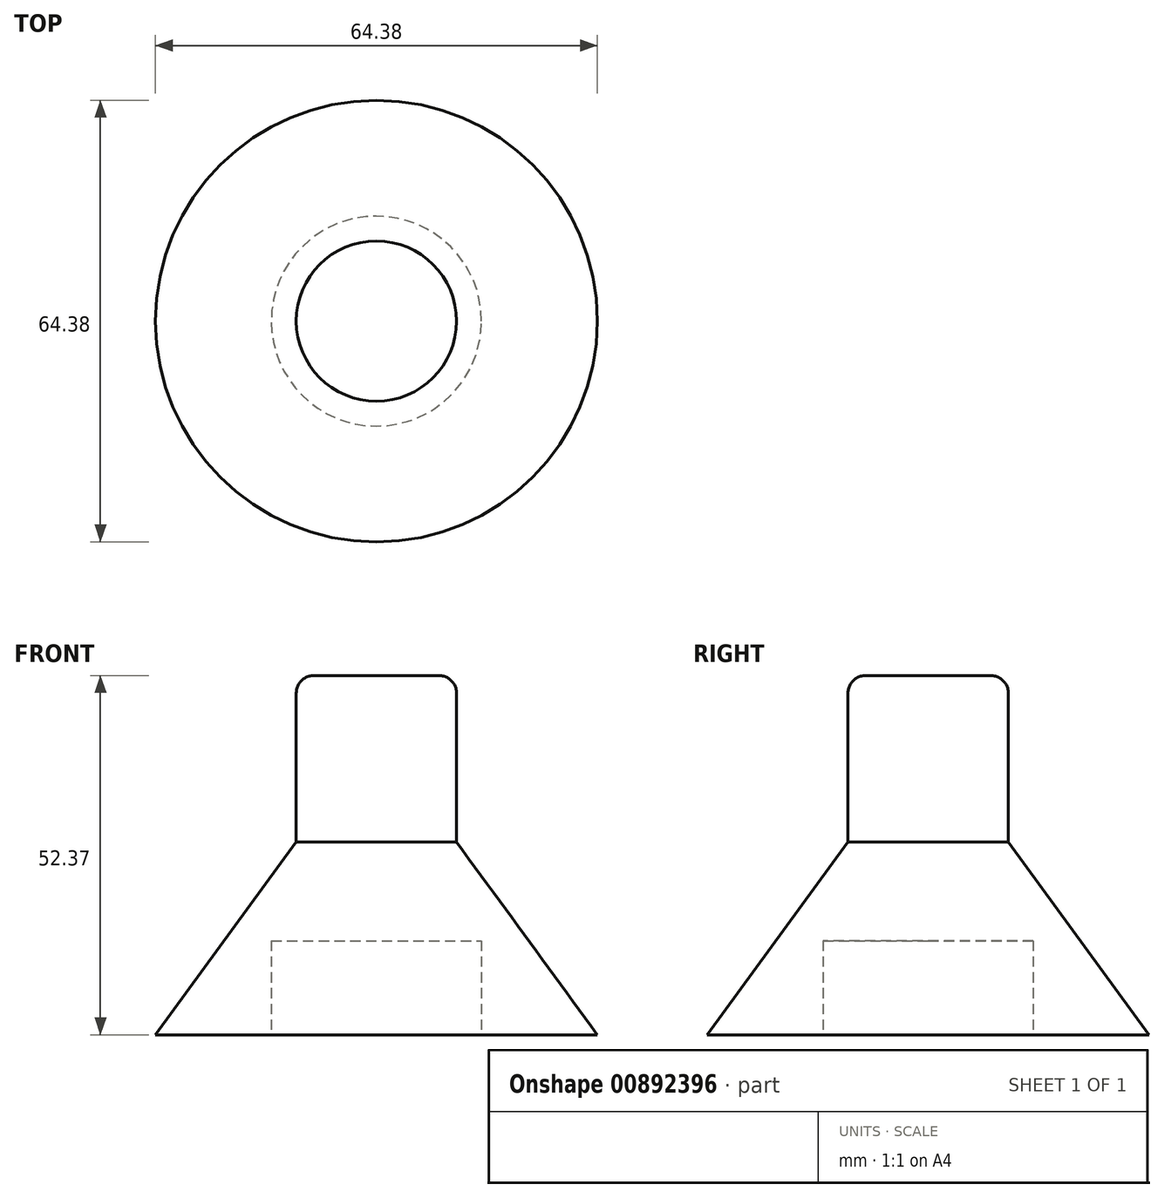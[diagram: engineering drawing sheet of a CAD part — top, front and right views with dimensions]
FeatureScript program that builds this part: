
annotation { "Feature Type Name" : "Feature", "Feature Type Description" : "" }
export const myFeature = defineFeature(function(context is Context, id is Id, definition is map)
    precondition{}
    {
        {
            var Q0;
            Q0=qCreatedBy(makeId("Front.planeOp"),FACE);
            var sketch = newSketch(context, id + "F0", { "sketchPlane" : qUnion([Q0])});
            skLineSegment(sketch, "E0", {"start": v(0, 0) * mm, "end": v(32.2, 0) * mm});
            skLineSegment(sketch, "E1", {"start": v(32.2, 0) * mm, "end": v(11.68, 28.1) * mm});
            skLineSegment(sketch, "E2", {"start": v(11.68, 28.1) * mm, "end": v(11.68, 49.83) * mm});
            skLineSegment(sketch, "E3", {"start": v(9.14, 52.37) * mm, "end": v(0, 52.37) * mm});
            skLineSegment(sketch, "E4", {"start": v(0, 52.37) * mm, "end": v(0, 0) * mm});
            skPoint(sketch, "E5.visualSharp", {"position": v(11.68, 52.37) * mm});
            skArc(sketch, "E5.filletArc", {"start": v(11.68, 49.83) * mm, "mid": v(10.93, 51.63) * mm, "end": v(9.14, 52.37) * mm});
            skPoint(sketch, "E6.end.orphan", {"position": v(-43.87, 52.37) * mm});
            skSolve(sketch);
        }
        {
            var Q0;
            Q0=makeQuery(id+"F0.imprint","IMPRINT",FACE,{"disambiguationData":[TD([[makeQuery(id+"F0.imprint","IMPRINT",EDGE,{"derivedFrom":sQuery(id+"F0.wireOp",EDGE,"E0")}),1.0]])]});
            var Q1;
            Q1=sQuery(id+"F0.wireOp",EDGE,"E4");
            revolve(context, id + "F1", {"surfaceOperationType" : NewSurfaceOperationType.NEW, "entities" : qUnion([Q0]), "axis" : qUnion([Q1]), "revolveType" : RevolveType.FULL});
        }
        {
            var Q0;
            Q0=makeQuery(id+"F1.opRevolve","SWEPT_FACE",FACE,{"disambiguationData":[OSD([sQuery(id+"F0.wireOp",EDGE,"E0")])]});
            var sketch = newSketch(context, id + "F2", { "sketchPlane" : qUnion([Q0])});
            skCircle(sketch, "E7", {"center": v(0, 0) * mm, "radius": 15.31 * mm});
            skSolve(sketch);
        }
        {
            var Q0;
            Q0 = qSketchRegion(id + "F2", true);
            extrude(context, id + "F3", {"entities" : qUnion([Q0]), "operationType" : NewBodyOperationType.REMOVE, "oppositeDirection" : true, "depth" : 13.72 * mm, "offsetDistance" : 25.4 * mm});
        }
    });
